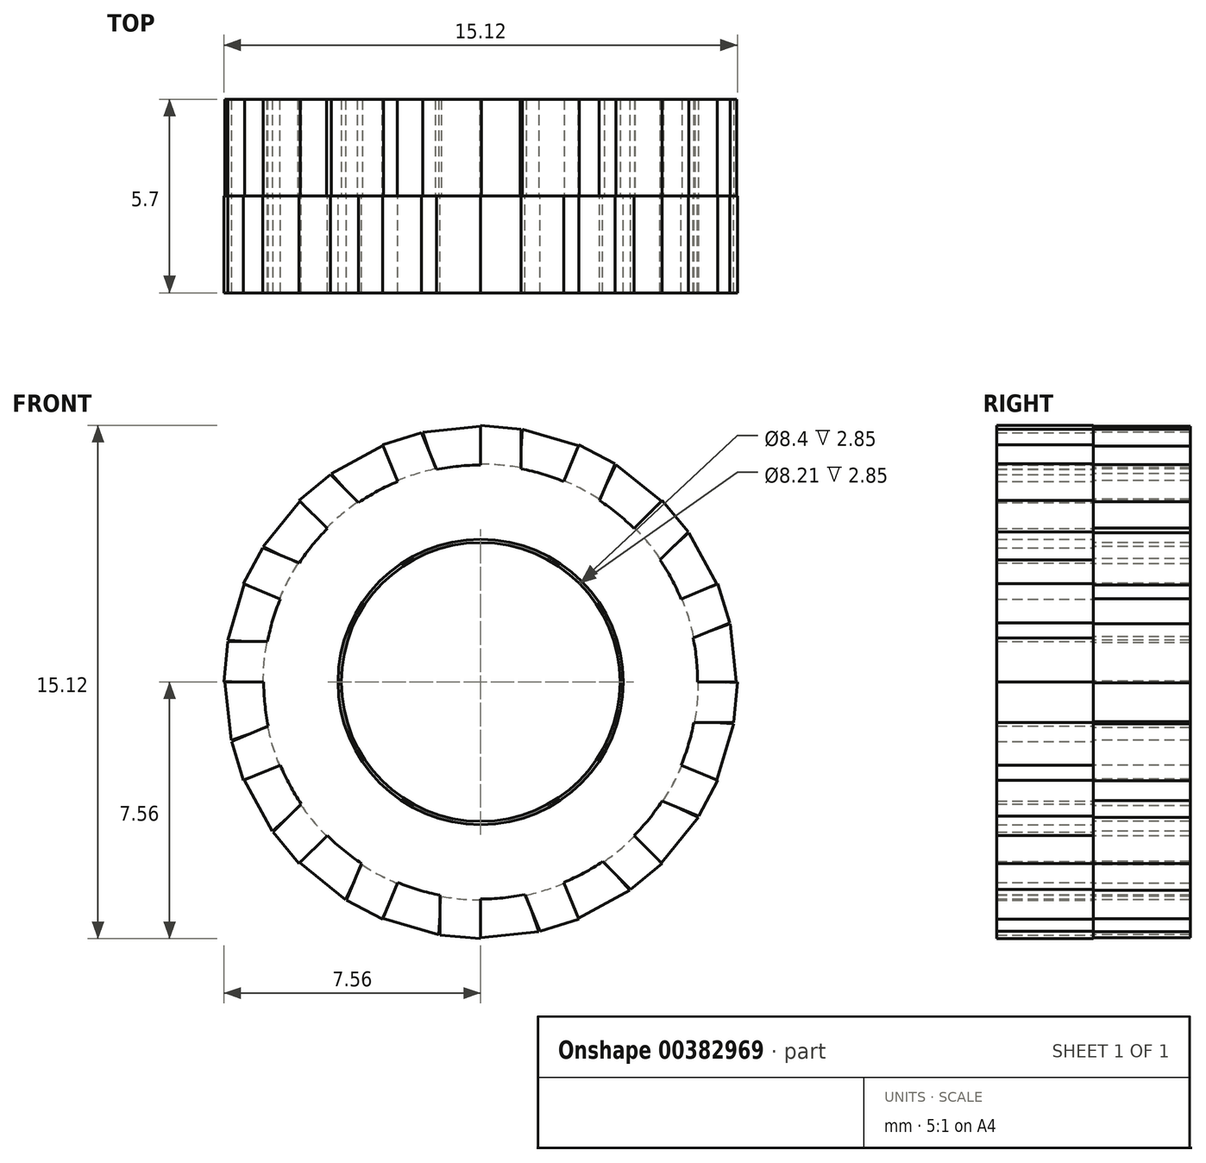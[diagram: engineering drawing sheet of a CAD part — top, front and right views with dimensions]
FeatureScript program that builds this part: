
annotation { "Feature Type Name" : "Feature", "Feature Type Description" : "" }
export const myFeature = defineFeature(function(context is Context, id is Id, definition is map)
    precondition{}
    {
        {
            var Q0;
            Q0=qCreatedBy(makeId("Front.planeOp"),FACE);
            var sketch = newSketch(context, id + "F0", { "sketchPlane" : qUnion([Q0])});
            skCircle(sketch, "E0", {"center": v(0, 0) * mm, "radius": 4.2 * mm});
            skArc(sketch, "E1", {"start": v(0, 6.39) * mm, "mid": v(-0.65, 6.36) * mm, "end": v(-1.3, 6.26) * mm});
            skLineSegment(sketch, "E2", {"start": v(0, 6.39) * mm, "end": v(0, 7.56) * mm});
            skLineSegment(sketch, "E3", {"start": v(0, 7.56) * mm, "end": v(1.2, 7.45) * mm});
            skPoint(sketch, "E4.end.orphan", {"position": v(1.2, 7.56) * mm});
            skLineSegment(sketch, "E5", {"start": v(1.2, 7.45) * mm, "end": v(1.2, 6.28) * mm});
            skLineSegment(sketch, "E6.1.0", {"start": v(-2.9, 6.98) * mm, "end": v(-1.75, 7.34) * mm});
            skLineSegment(sketch, "E6.1.1", {"start": v(-2.45, 5.9) * mm, "end": v(-2.9, 6.98) * mm});
            skLineSegment(sketch, "E6.1.2", {"start": v(-1.75, 7.34) * mm, "end": v(-1.3, 6.26) * mm});
            skLineSegment(sketch, "E6.2.0", {"start": v(-5.35, 5.35) * mm, "end": v(-4.42, 6.11) * mm});
            skLineSegment(sketch, "E6.2.1", {"start": v(-4.52, 4.52) * mm, "end": v(-5.35, 5.35) * mm});
            skLineSegment(sketch, "E6.2.2", {"start": v(-4.42, 6.11) * mm, "end": v(-3.6, 5.28) * mm});
            skLineSegment(sketch, "E6.3.0", {"start": v(-6.98, 2.9) * mm, "end": v(-6.42, 3.95) * mm});
            skLineSegment(sketch, "E6.3.1", {"start": v(-5.9, 2.45) * mm, "end": v(-6.98, 2.9) * mm});
            skLineSegment(sketch, "E6.3.2", {"start": v(-6.42, 3.95) * mm, "end": v(-5.34, 3.5) * mm});
            skLineSegment(sketch, "E6.4.0", {"start": v(-7.56, 0) * mm, "end": v(-7.45, 1.2) * mm});
            skLineSegment(sketch, "E6.4.1", {"start": v(-6.39, 0) * mm, "end": v(-7.56, 0) * mm});
            skLineSegment(sketch, "E6.4.2", {"start": v(-7.45, 1.2) * mm, "end": v(-6.28, 1.2) * mm});
            skLineSegment(sketch, "E6.5.0", {"start": v(-6.98, -2.9) * mm, "end": v(-7.34, -1.75) * mm});
            skLineSegment(sketch, "E6.5.1", {"start": v(-5.9, -2.45) * mm, "end": v(-6.98, -2.9) * mm});
            skLineSegment(sketch, "E6.5.2", {"start": v(-7.34, -1.75) * mm, "end": v(-6.26, -1.3) * mm});
            skLineSegment(sketch, "E6.6.0", {"start": v(-5.35, -5.35) * mm, "end": v(-6.11, -4.42) * mm});
            skLineSegment(sketch, "E6.6.1", {"start": v(-4.52, -4.52) * mm, "end": v(-5.35, -5.35) * mm});
            skLineSegment(sketch, "E6.6.2", {"start": v(-6.11, -4.42) * mm, "end": v(-5.28, -3.6) * mm});
            skLineSegment(sketch, "E6.7.0", {"start": v(-2.9, -6.98) * mm, "end": v(-3.95, -6.42) * mm});
            skLineSegment(sketch, "E6.7.1", {"start": v(-2.45, -5.9) * mm, "end": v(-2.9, -6.98) * mm});
            skLineSegment(sketch, "E6.7.2", {"start": v(-3.95, -6.42) * mm, "end": v(-3.5, -5.34) * mm});
            skLineSegment(sketch, "E6.8.0", {"start": v(0, -7.56) * mm, "end": v(-1.2, -7.45) * mm});
            skLineSegment(sketch, "E6.8.1", {"start": v(0, -6.39) * mm, "end": v(0, -7.56) * mm});
            skLineSegment(sketch, "E6.8.2", {"start": v(-1.2, -7.45) * mm, "end": v(-1.2, -6.28) * mm});
            skLineSegment(sketch, "E6.9.0", {"start": v(2.9, -6.98) * mm, "end": v(1.75, -7.34) * mm});
            skLineSegment(sketch, "E6.9.1", {"start": v(2.45, -5.9) * mm, "end": v(2.9, -6.98) * mm});
            skLineSegment(sketch, "E6.9.2", {"start": v(1.75, -7.34) * mm, "end": v(1.3, -6.26) * mm});
            skLineSegment(sketch, "E6.10.0", {"start": v(5.35, -5.35) * mm, "end": v(4.42, -6.11) * mm});
            skLineSegment(sketch, "E6.10.1", {"start": v(4.52, -4.52) * mm, "end": v(5.35, -5.35) * mm});
            skLineSegment(sketch, "E6.10.2", {"start": v(4.42, -6.11) * mm, "end": v(3.6, -5.28) * mm});
            skLineSegment(sketch, "E6.11.0", {"start": v(6.98, -2.9) * mm, "end": v(6.42, -3.95) * mm});
            skLineSegment(sketch, "E6.11.1", {"start": v(5.9, -2.45) * mm, "end": v(6.98, -2.9) * mm});
            skLineSegment(sketch, "E6.11.2", {"start": v(6.42, -3.95) * mm, "end": v(5.34, -3.5) * mm});
            skLineSegment(sketch, "E6.12.0", {"start": v(7.56, 0) * mm, "end": v(7.45, -1.2) * mm});
            skLineSegment(sketch, "E6.12.1", {"start": v(6.39, 0) * mm, "end": v(7.56, 0) * mm});
            skLineSegment(sketch, "E6.12.2", {"start": v(7.45, -1.2) * mm, "end": v(6.28, -1.2) * mm});
            skLineSegment(sketch, "E6.13.0", {"start": v(6.98, 2.9) * mm, "end": v(7.34, 1.75) * mm});
            skLineSegment(sketch, "E6.13.1", {"start": v(5.9, 2.45) * mm, "end": v(6.98, 2.9) * mm});
            skLineSegment(sketch, "E6.13.2", {"start": v(7.34, 1.75) * mm, "end": v(6.26, 1.3) * mm});
            skLineSegment(sketch, "E6.14.0", {"start": v(5.35, 5.35) * mm, "end": v(6.11, 4.42) * mm});
            skLineSegment(sketch, "E6.14.1", {"start": v(4.52, 4.52) * mm, "end": v(5.35, 5.35) * mm});
            skLineSegment(sketch, "E6.14.2", {"start": v(6.11, 4.42) * mm, "end": v(5.28, 3.6) * mm});
            skLineSegment(sketch, "E6.15.0", {"start": v(2.9, 6.98) * mm, "end": v(3.95, 6.42) * mm});
            skLineSegment(sketch, "E6.15.1", {"start": v(2.45, 5.9) * mm, "end": v(2.9, 6.98) * mm});
            skLineSegment(sketch, "E6.15.2", {"start": v(3.95, 6.42) * mm, "end": v(3.5, 5.34) * mm});
            skArc(sketch, "E7.trimOffspring", {"start": v(2.45, 5.9) * mm, "mid": v(1.83, 6.12) * mm, "end": v(1.2, 6.28) * mm});
            skArc(sketch, "E8.trimOffspring", {"start": v(4.52, 4.52) * mm, "mid": v(4.03, 4.96) * mm, "end": v(3.5, 5.34) * mm});
            skArc(sketch, "E9.trimOffspring", {"start": v(5.9, 2.45) * mm, "mid": v(5.62, 3.04) * mm, "end": v(5.28, 3.6) * mm});
            skArc(sketch, "E10.trimOffspring", {"start": v(6.39, 0) * mm, "mid": v(6.36, 0.65) * mm, "end": v(6.26, 1.3) * mm});
            skArc(sketch, "E11.trimOffspring", {"start": v(5.9, -2.45) * mm, "mid": v(6.12, -1.83) * mm, "end": v(6.28, -1.2) * mm});
            skArc(sketch, "E12.trimOffspring", {"start": v(4.52, -4.52) * mm, "mid": v(4.96, -4.03) * mm, "end": v(5.34, -3.5) * mm});
            skArc(sketch, "E13.trimOffspring", {"start": v(0, -6.39) * mm, "mid": v(0.65, -6.36) * mm, "end": v(1.3, -6.26) * mm});
            skArc(sketch, "E14.trimOffspring", {"start": v(2.45, -5.9) * mm, "mid": v(3.04, -5.62) * mm, "end": v(3.6, -5.28) * mm});
            skArc(sketch, "E15.trimOffspring", {"start": v(-2.45, -5.9) * mm, "mid": v(-1.83, -6.12) * mm, "end": v(-1.2, -6.28) * mm});
            skArc(sketch, "E16.trimOffspring", {"start": v(-4.52, -4.52) * mm, "mid": v(-4.03, -4.96) * mm, "end": v(-3.5, -5.34) * mm});
            skArc(sketch, "E17.trimOffspring", {"start": v(-5.9, -2.45) * mm, "mid": v(-5.62, -3.04) * mm, "end": v(-5.28, -3.6) * mm});
            skArc(sketch, "E18.trimOffspring", {"start": v(-6.39, 0) * mm, "mid": v(-6.36, -0.65) * mm, "end": v(-6.26, -1.3) * mm});
            skArc(sketch, "E19.trimOffspring", {"start": v(-5.9, 2.45) * mm, "mid": v(-6.12, 1.83) * mm, "end": v(-6.28, 1.2) * mm});
            skArc(sketch, "E20.trimOffspring", {"start": v(-4.52, 4.52) * mm, "mid": v(-4.96, 4.03) * mm, "end": v(-5.34, 3.5) * mm});
            skArc(sketch, "E21.trimOffspring", {"start": v(-2.45, 5.9) * mm, "mid": v(-3.04, 5.62) * mm, "end": v(-3.6, 5.28) * mm});
            skSolve(sketch);
        }
        {
            var Q0;
            Q0=qSketchRegion(id+"F0",true);
            var Q1;
            Q1=makeQuery(id+"F0.imprint","IMPRINT",FACE,{"disambiguationData":[TD([[makeQuery(id+"F0.imprint","IMPRINT",EDGE,{"derivedFrom":sQuery(id+"F0.wireOp",EDGE,"E0")}),-1.0]])]});
            extrude(context, id + "F1", {"entities" : qUnion([Q0, Q1]), "depth" : 2.85 * mm});
        }
        {
            var Q0;
            Q0=qCreatedBy(makeId("Front.planeOp"),FACE);
            var sketch = newSketch(context, id + "F2", { "sketchPlane" : qUnion([Q0])});
            skCircle(sketch, "E22", {"center": v(0, 0) * mm, "radius": 4.1 * mm});
            skArc(sketch, "E23", {"start": v(-3.64, 5.28) * mm, "mid": v(-4.1, 4.93) * mm, "end": v(-4.54, 4.54) * mm});
            skLineSegment(sketch, "E24", {"start": v(-2.46, 5.93) * mm, "end": v(-2.86, 6.97) * mm});
            skLineSegment(sketch, "E25", {"start": v(-3.64, 5.28) * mm, "end": v(-4.4, 6.13) * mm});
            skLineSegment(sketch, "E26", {"start": v(-4.4, 6.13) * mm, "end": v(-2.86, 6.97) * mm});
            skLineSegment(sketch, "E27.1.0", {"start": v(-6.4, 3.99) * mm, "end": v(-5.3, 5.35) * mm});
            skLineSegment(sketch, "E27.1.1", {"start": v(-5.38, 3.49) * mm, "end": v(-6.4, 3.99) * mm});
            skLineSegment(sketch, "E27.1.2", {"start": v(-4.54, 4.54) * mm, "end": v(-5.3, 5.35) * mm});
            skLineSegment(sketch, "E27.2.0", {"start": v(-7.44, 1.23) * mm, "end": v(-6.95, 2.9) * mm});
            skLineSegment(sketch, "E27.2.1", {"start": v(-6.3, 1.16) * mm, "end": v(-7.44, 1.23) * mm});
            skLineSegment(sketch, "E27.2.2", {"start": v(-5.93, 2.45) * mm, "end": v(-6.95, 2.9) * mm});
            skLineSegment(sketch, "E28.1.3.0", {"start": v(-7.35, -1.71) * mm, "end": v(-7.53, 0.03) * mm});
            skLineSegment(sketch, "E28.3.3.0", {"start": v(-6.27, -1.34) * mm, "end": v(-7.35, -1.71) * mm});
            skLineSegment(sketch, "E28.6.3.0", {"start": v(-6.42, 0) * mm, "end": v(-7.53, 0.03) * mm});
            skLineSegment(sketch, "E28.1.4.0", {"start": v(-6.13, -4.4) * mm, "end": v(-6.97, -2.86) * mm});
            skLineSegment(sketch, "E28.3.4.0", {"start": v(-5.28, -3.64) * mm, "end": v(-6.13, -4.4) * mm});
            skLineSegment(sketch, "E28.6.4.0", {"start": v(-5.93, -2.46) * mm, "end": v(-6.97, -2.86) * mm});
            skLineSegment(sketch, "E28.1.5.0", {"start": v(-3.99, -6.4) * mm, "end": v(-5.35, -5.3) * mm});
            skLineSegment(sketch, "E28.3.5.0", {"start": v(-3.49, -5.38) * mm, "end": v(-3.99, -6.4) * mm});
            skLineSegment(sketch, "E28.6.5.0", {"start": v(-4.54, -4.54) * mm, "end": v(-5.35, -5.3) * mm});
            skLineSegment(sketch, "E28.1.6.0", {"start": v(-1.23, -7.44) * mm, "end": v(-2.9, -6.95) * mm});
            skLineSegment(sketch, "E28.3.6.0", {"start": v(-1.16, -6.3) * mm, "end": v(-1.23, -7.44) * mm});
            skLineSegment(sketch, "E28.6.6.0", {"start": v(-2.45, -5.93) * mm, "end": v(-2.9, -6.95) * mm});
            skLineSegment(sketch, "E28.1.7.0", {"start": v(1.71, -7.35) * mm, "end": v(-0.03, -7.53) * mm});
            skLineSegment(sketch, "E28.3.7.0", {"start": v(1.34, -6.27) * mm, "end": v(1.71, -7.35) * mm});
            skLineSegment(sketch, "E28.6.7.0", {"start": v(0, -6.42) * mm, "end": v(-0.03, -7.53) * mm});
            skLineSegment(sketch, "E28.1.8.0", {"start": v(4.4, -6.13) * mm, "end": v(2.86, -6.97) * mm});
            skLineSegment(sketch, "E28.3.8.0", {"start": v(3.64, -5.28) * mm, "end": v(4.4, -6.13) * mm});
            skLineSegment(sketch, "E28.6.8.0", {"start": v(2.46, -5.93) * mm, "end": v(2.86, -6.97) * mm});
            skLineSegment(sketch, "E28.1.9.0", {"start": v(6.4, -3.99) * mm, "end": v(5.3, -5.35) * mm});
            skLineSegment(sketch, "E28.3.9.0", {"start": v(5.38, -3.49) * mm, "end": v(6.4, -3.99) * mm});
            skLineSegment(sketch, "E28.6.9.0", {"start": v(4.54, -4.54) * mm, "end": v(5.3, -5.35) * mm});
            skLineSegment(sketch, "E28.1.10.0", {"start": v(7.44, -1.23) * mm, "end": v(6.95, -2.9) * mm});
            skLineSegment(sketch, "E28.3.10.0", {"start": v(6.3, -1.16) * mm, "end": v(7.44, -1.23) * mm});
            skLineSegment(sketch, "E28.6.10.0", {"start": v(5.93, -2.45) * mm, "end": v(6.95, -2.9) * mm});
            skLineSegment(sketch, "E28.1.11.0", {"start": v(7.35, 1.71) * mm, "end": v(7.53, -0.03) * mm});
            skLineSegment(sketch, "E28.3.11.0", {"start": v(6.27, 1.34) * mm, "end": v(7.35, 1.71) * mm});
            skLineSegment(sketch, "E28.6.11.0", {"start": v(6.42, 0) * mm, "end": v(7.53, -0.03) * mm});
            skLineSegment(sketch, "E28.1.12.0", {"start": v(6.13, 4.4) * mm, "end": v(6.97, 2.86) * mm});
            skLineSegment(sketch, "E28.3.12.0", {"start": v(5.28, 3.64) * mm, "end": v(6.13, 4.4) * mm});
            skLineSegment(sketch, "E28.6.12.0", {"start": v(5.93, 2.46) * mm, "end": v(6.97, 2.86) * mm});
            skLineSegment(sketch, "E28.1.13.0", {"start": v(3.99, 6.4) * mm, "end": v(5.35, 5.3) * mm});
            skLineSegment(sketch, "E28.3.13.0", {"start": v(3.49, 5.38) * mm, "end": v(3.99, 6.4) * mm});
            skLineSegment(sketch, "E28.6.13.0", {"start": v(4.54, 4.54) * mm, "end": v(5.35, 5.3) * mm});
            skLineSegment(sketch, "E28.1.14.0", {"start": v(1.23, 7.44) * mm, "end": v(2.9, 6.95) * mm});
            skLineSegment(sketch, "E28.3.14.0", {"start": v(1.16, 6.3) * mm, "end": v(1.23, 7.44) * mm});
            skLineSegment(sketch, "E28.6.14.0", {"start": v(2.45, 5.93) * mm, "end": v(2.9, 6.95) * mm});
            skLineSegment(sketch, "E28.1.15.0", {"start": v(-1.71, 7.35) * mm, "end": v(0.03, 7.53) * mm});
            skLineSegment(sketch, "E28.3.15.0", {"start": v(-1.34, 6.27) * mm, "end": v(-1.71, 7.35) * mm});
            skLineSegment(sketch, "E28.6.15.0", {"start": v(0, 6.42) * mm, "end": v(0.03, 7.53) * mm});
            skArc(sketch, "E29.trimOffspring", {"start": v(-1.34, 6.27) * mm, "mid": v(-1.9, 6.13) * mm, "end": v(-2.46, 5.93) * mm});
            skArc(sketch, "E30.trimOffspring", {"start": v(1.16, 6.3) * mm, "mid": v(0.58, 6.39) * mm, "end": v(0, 6.42) * mm});
            skArc(sketch, "E31.trimOffspring", {"start": v(3.49, 5.38) * mm, "mid": v(2.98, 5.68) * mm, "end": v(2.45, 5.93) * mm});
            skArc(sketch, "E32.trimOffspring", {"start": v(5.28, 3.64) * mm, "mid": v(4.93, 4.1) * mm, "end": v(4.54, 4.54) * mm});
            skArc(sketch, "E33.trimOffspring", {"start": v(6.27, 1.34) * mm, "mid": v(6.13, 1.9) * mm, "end": v(5.93, 2.46) * mm});
            skArc(sketch, "E34.trimOffspring", {"start": v(6.3, -1.16) * mm, "mid": v(6.39, -0.58) * mm, "end": v(6.42, 0) * mm});
            skArc(sketch, "E35.trimOffspring", {"start": v(5.38, -3.49) * mm, "mid": v(5.68, -2.98) * mm, "end": v(5.93, -2.45) * mm});
            skArc(sketch, "E36.trimOffspring", {"start": v(3.64, -5.28) * mm, "mid": v(4.1, -4.93) * mm, "end": v(4.54, -4.54) * mm});
            skArc(sketch, "E37.trimOffspring", {"start": v(1.34, -6.27) * mm, "mid": v(1.9, -6.13) * mm, "end": v(2.46, -5.93) * mm});
            skArc(sketch, "E38.trimOffspring", {"start": v(-1.16, -6.3) * mm, "mid": v(-0.58, -6.39) * mm, "end": v(0, -6.42) * mm});
            skArc(sketch, "E39.trimOffspring", {"start": v(-3.49, -5.38) * mm, "mid": v(-2.98, -5.68) * mm, "end": v(-2.45, -5.93) * mm});
            skArc(sketch, "E40.trimOffspring", {"start": v(-5.28, -3.64) * mm, "mid": v(-4.93, -4.1) * mm, "end": v(-4.54, -4.54) * mm});
            skArc(sketch, "E41.trimOffspring", {"start": v(-6.27, -1.34) * mm, "mid": v(-6.13, -1.9) * mm, "end": v(-5.93, -2.46) * mm});
            skArc(sketch, "E42.trimOffspring", {"start": v(-6.3, 1.16) * mm, "mid": v(-6.39, 0.58) * mm, "end": v(-6.42, 0) * mm});
            skArc(sketch, "E43.trimOffspring", {"start": v(-5.38, 3.49) * mm, "mid": v(-5.68, 2.98) * mm, "end": v(-5.93, 2.45) * mm});
            skSolve(sketch);
        }
        {
            var Q0;
            Q0=makeQuery(id+"F2.imprint","IMPRINT",FACE,{"disambiguationData":[TD([[makeQuery(id+"F2.imprint","IMPRINT",EDGE,{"derivedFrom":sQuery(id+"F2.wireOp",EDGE,"E22")}),-1.0]])]});
            extrude(context, id + "F3", {"entities" : qUnion([Q0]), "operationType" : NewBodyOperationType.ADD, "oppositeDirection" : true, "depth" : 2.85 * mm});
        }
    });
